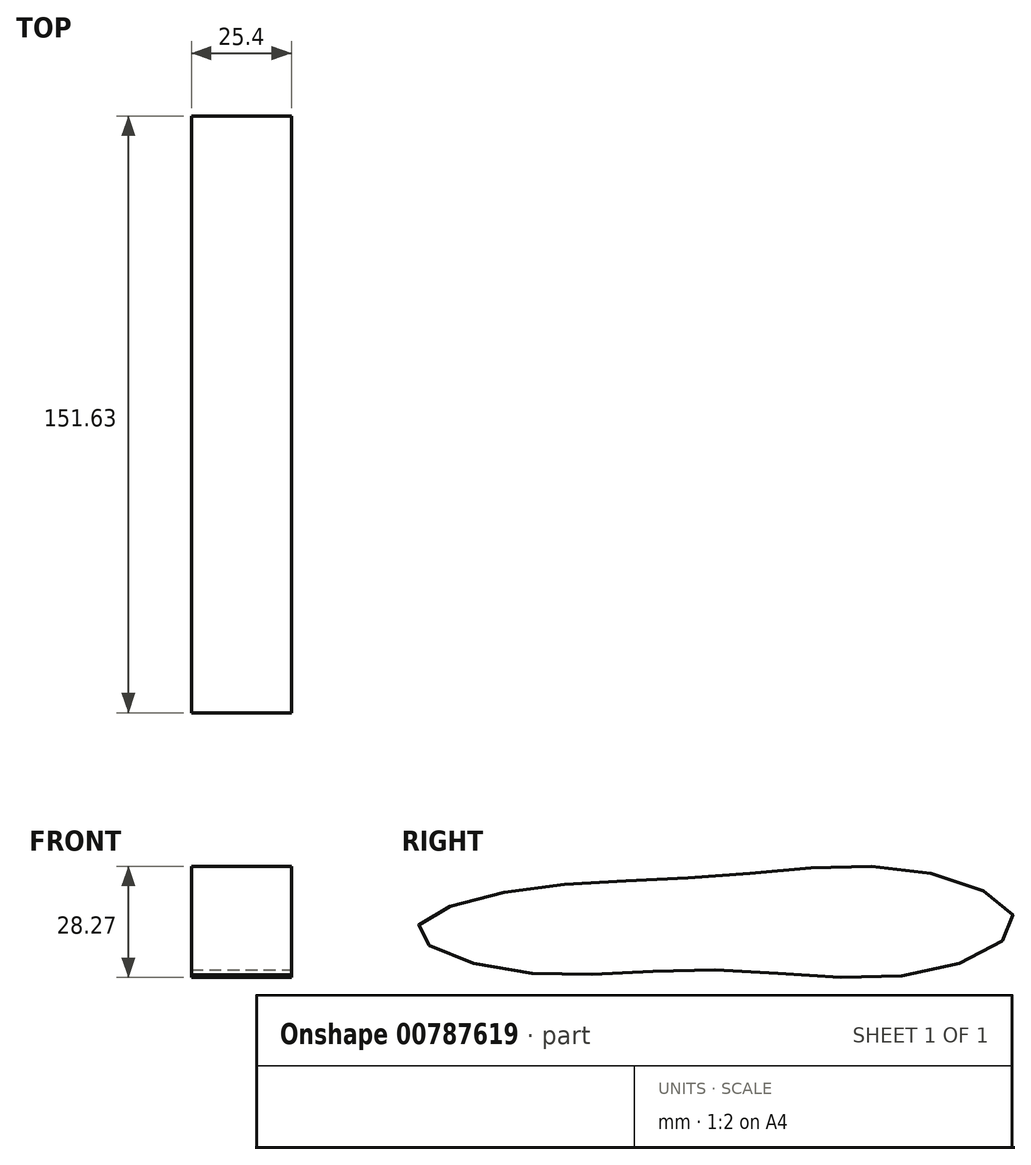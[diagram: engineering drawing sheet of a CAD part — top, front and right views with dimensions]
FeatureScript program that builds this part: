
annotation { "Feature Type Name" : "Feature", "Feature Type Description" : "" }
export const myFeature = defineFeature(function(context is Context, id is Id, definition is map)
    precondition{}
    {
        {
            var Q0;
            Q0=qCreatedBy(makeId("Right.planeOp"),FACE);
            var sketch = newSketch(context, id + "F0", { "sketchPlane" : qUnion([Q0])});
            skFitSpline(sketch, "E0", {"points": [v(0, -75.95) * mm, v(-51.9, -76.23) * mm, v(-75.68, -65.88) * mm, v(-53.02, -56.1) * mm, v(0, -52.17) * mm, v(51.32, -50.78) * mm, v(75.94, -63.36) * mm, v(53.56, -76.51) * mm, v(0, -75.95) * mm]});
            skSolve(sketch);
        }
        {
            var Q0;
            Q0=sQuery(id+"F0.wireOp",EDGE,"E0");
            extrude(context, id + "F1", {"bodyType" : ToolBodyType.SURFACE, "surfaceEntities" : qUnion([Q0]), "depth" : 25.4 * mm, "offsetDistance" : 25.4 * mm});
        }
    });
